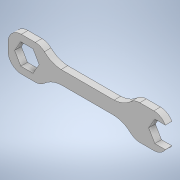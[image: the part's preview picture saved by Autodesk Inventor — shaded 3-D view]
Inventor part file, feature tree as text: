
AUTODESK INVENTOR PART (.ipt)
format: ipt  version: 2020.2 (Build 242310000, 310)  size: 161,280 bytes
history: native  units: in
note: dims shown in document units (in); Inventor stores cm internally (conversion verified against a paired STEP export)
features: extrude x1, sketch x1
ambient origin geometry x8: Origin, YZ Plane, XZ Plane, XY Plane, X Axis, Y Axis, Z Axis, Center Point
bodies: Solid1 (feature_tree)
feature tree (2):
  extrude  "Extrusion1"  Depth=0.8in
  sketch  "Sketch1"  dims[d3=0.25in d4=0.8in d8=1.75in d10=1.0in d11=1.0in d15=0.5in d16=0.5in d17=0.5in d18=0.25in d19=0.0in]
